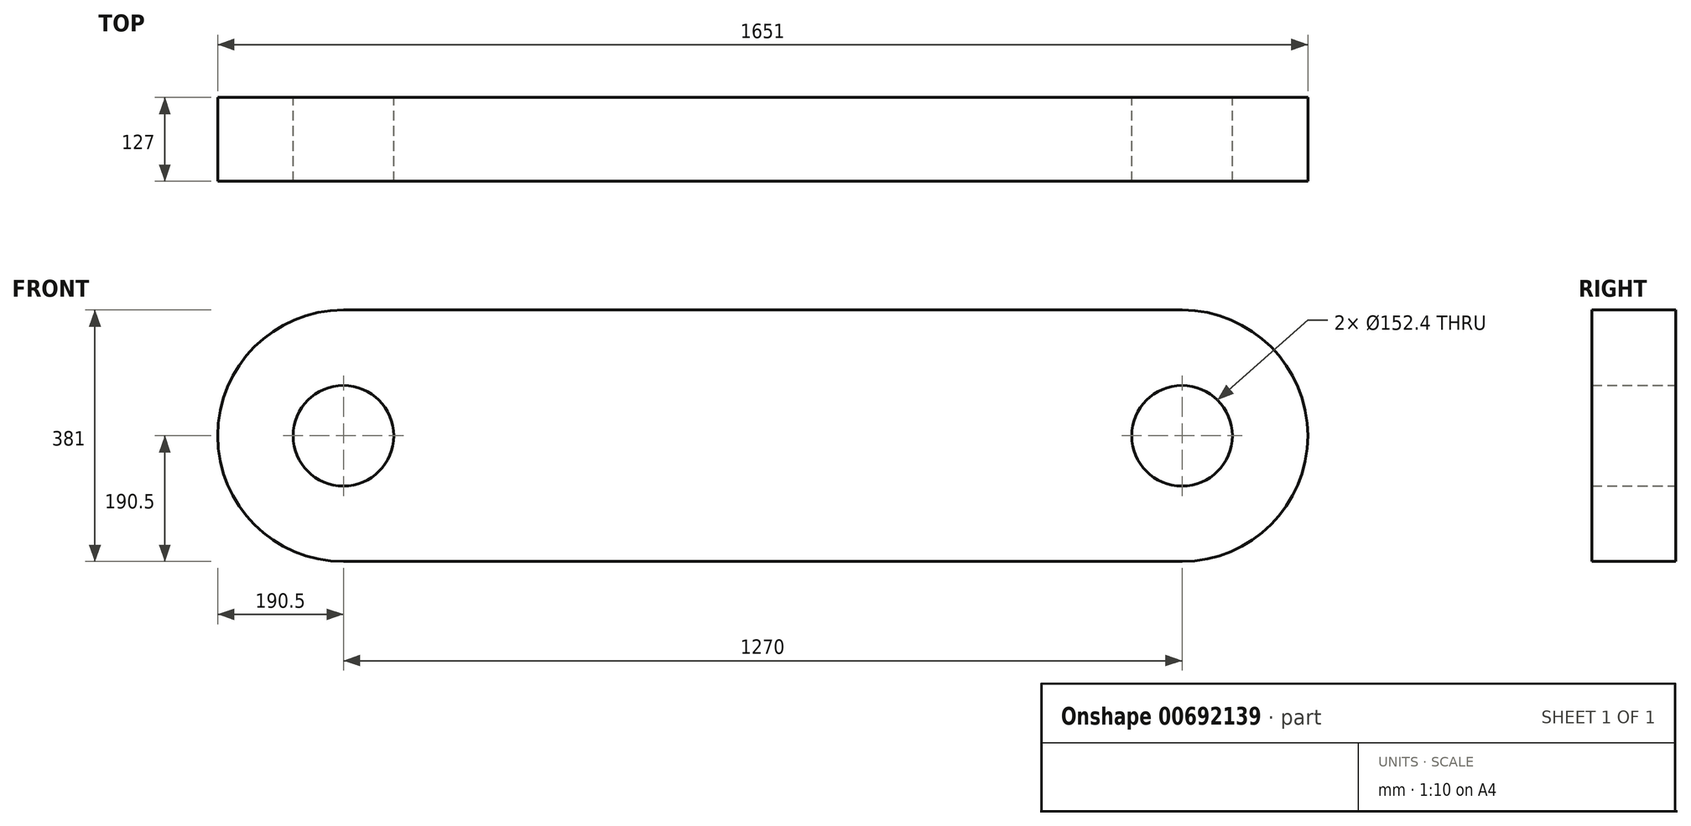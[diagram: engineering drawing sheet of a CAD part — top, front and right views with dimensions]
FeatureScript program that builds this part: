
annotation { "Feature Type Name" : "Feature", "Feature Type Description" : "" }
export const myFeature = defineFeature(function(context is Context, id is Id, definition is map)
    precondition{}
    {
        {
            var Q0;
            Q0=qCreatedBy(makeId("Front.planeOp"),FACE);
            var sketch = newSketch(context, id + "F0", { "sketchPlane" : qUnion([Q0])});
            skLineSegment(sketch, "E0.bottom", {"start": v(-635, 190.5) * mm, "end": v(635, 190.5) * mm});
            skLineSegment(sketch, "E0.top", {"start": v(-635, -190.5) * mm, "end": v(635, -190.5) * mm});
            skLineSegment(sketch, "E0.left", {"start": v(-635, 190.5) * mm, "end": v(-635, -190.5) * mm, "construction": true});
            skLineSegment(sketch, "E0.right", {"start": v(635, 190.5) * mm, "end": v(635, -190.5) * mm, "construction": true});
            skArc(sketch, "E1", {"start": v(-635, 190.5) * mm, "mid": v(-825.5, 0) * mm, "end": v(-635, -190.5) * mm});
            skArc(sketch, "E2.MirrorCS", {"start": v(635, 190.5) * mm, "mid": v(825.5, 0) * mm, "end": v(635, -190.5) * mm});
            skCircle(sketch, "E3", {"center": v(-635, 0) * mm, "radius": 76.2 * mm});
            skCircle(sketch, "E4", {"center": v(635, 0) * mm, "radius": 76.2 * mm});
            skSolve(sketch);
        }
        {
            var Q0;
            Q0=qSketchRegion(id+"F0",true);
            extrude(context, id + "F1", {"entities" : qUnion([Q0]), "depth" : 127 * mm, "offsetDistance" : 25.4 * mm});
        }
    });
